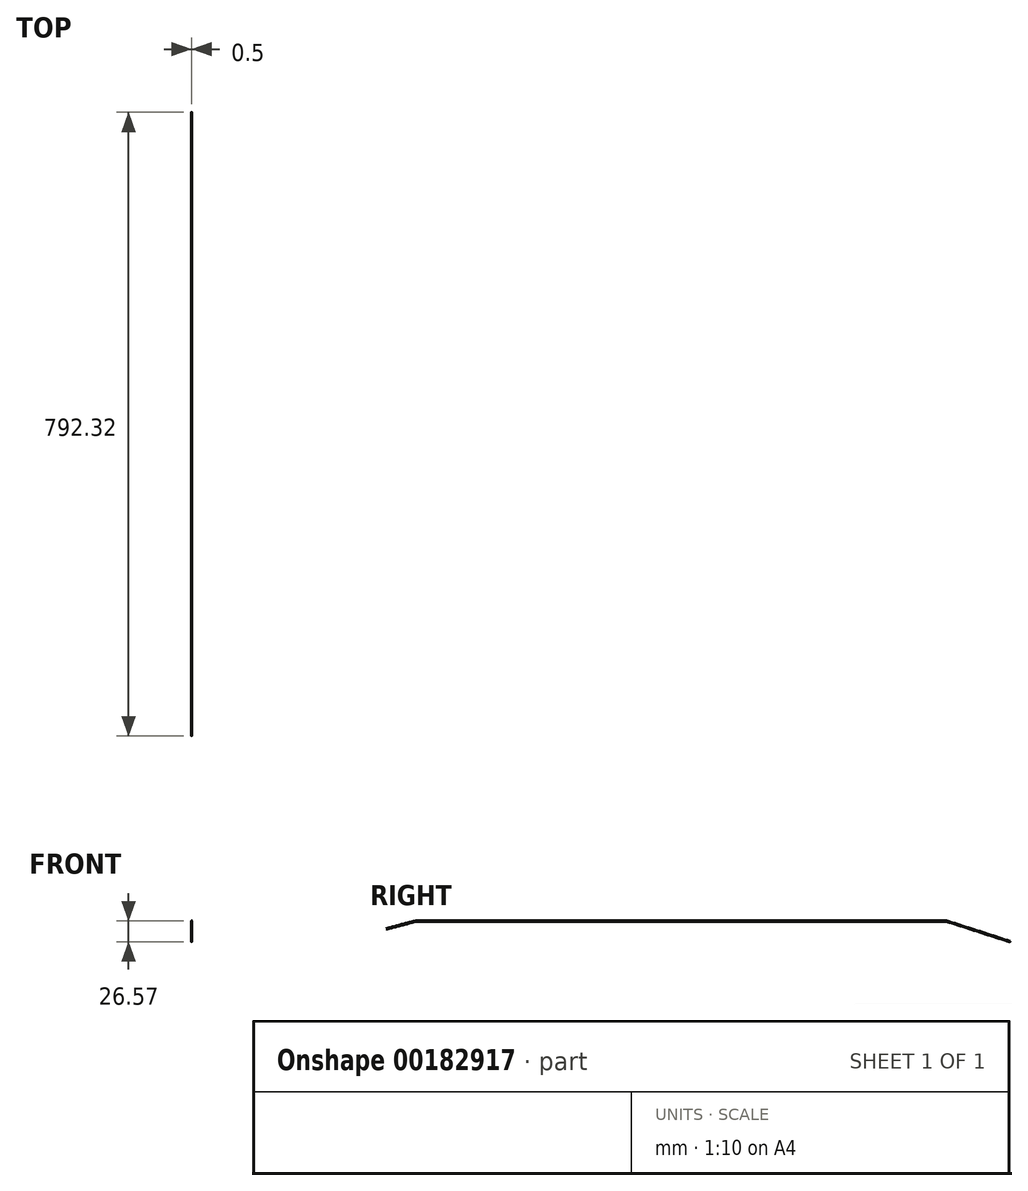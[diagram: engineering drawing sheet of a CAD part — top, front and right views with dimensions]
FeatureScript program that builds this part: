
annotation { "Feature Type Name" : "Feature", "Feature Type Description" : "" }
export const myFeature = defineFeature(function(context is Context, id is Id, definition is map)
    precondition{}
    {
        {
            var Q0;
            Q0=qCreatedBy(makeId("Front.planeOp"),FACE);
            var sketch = newSketch(context, id + "F0", { "sketchPlane" : qUnion([Q0])});
            skCircle(sketch, "E0", {"center": v(0, 0) * mm, "radius": 0.25 * mm});
            skSolve(sketch);
        }
        {
            var Q0;
            Q0=qCreatedBy(makeId("Right.planeOp"),FACE);
            var sketch = newSketch(context, id + "F1", { "sketchPlane" : qUnion([Q0])});
            skLineSegment(sketch, "E1", {"start": v(0, 0) * mm, "end": v(37.7, 9.97) * mm});
            skLineSegment(sketch, "E2", {"start": v(37.7, 9.97) * mm, "end": v(711.7, 9.97) * mm});
            skLineSegment(sketch, "E3", {"start": v(711.7, 9.97) * mm, "end": v(792.19, -16.15) * mm});
            skSolve(sketch);
        }
        {
            var Q0;
            Q0 = qSketchRegion(id + "F0", true);
            var Q1;
            Q1 = qConstructionFilter(qBodyType(qCreatedBy(id + "F1" ,EDGE), BodyType.WIRE), ConstructionObject.NO);
            sweep(context, id + "F2", {"profiles" : qUnion([Q0]), "path" : qUnion([Q1])});
        }
    });
